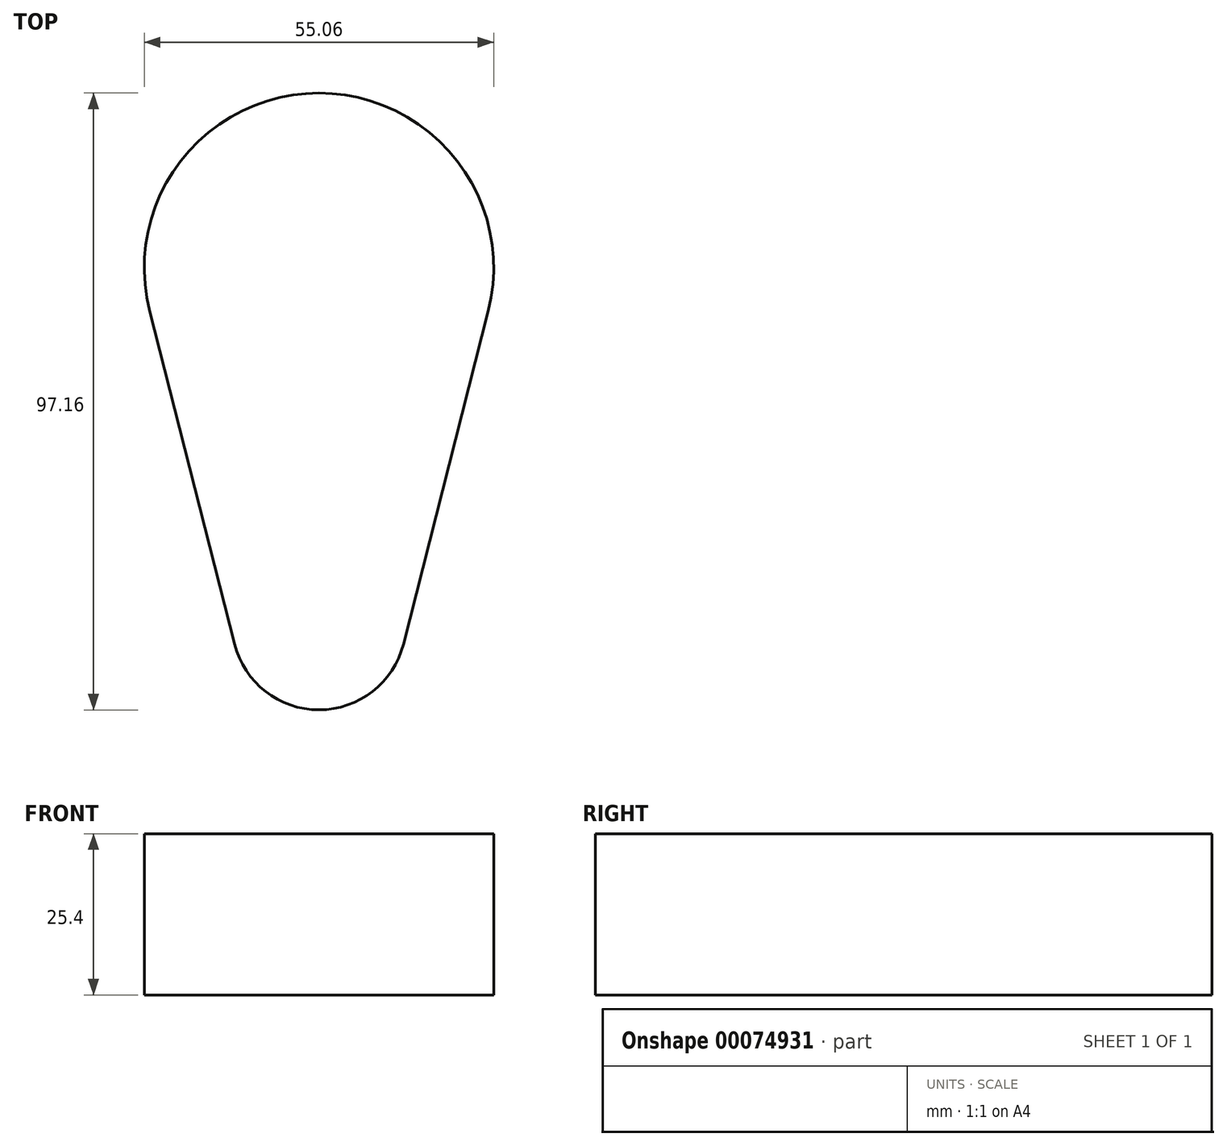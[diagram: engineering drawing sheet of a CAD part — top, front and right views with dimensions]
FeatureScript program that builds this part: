
annotation { "Feature Type Name" : "Feature", "Feature Type Description" : "" }
export const myFeature = defineFeature(function(context is Context, id is Id, definition is map)
    precondition{}
    {
        {
            var Q0;
            Q0=qCreatedBy(makeId("Top.planeOp"),FACE);
            var sketch = newSketch(context, id + "F0", { "sketchPlane" : qUnion([Q0])});
            skArc(sketch, "E0", {"start": v(-13.3, -59.29) * mm, "mid": v(0, -69.63) * mm, "end": v(13.3, -59.29) * mm});
            skLineSegment(sketch, "E1", {"start": v(26.68, -6.8) * mm, "end": v(13.3, -59.29) * mm});
            skLineSegment(sketch, "E2", {"start": v(-13.3, -59.29) * mm, "end": v(-26.68, -6.8) * mm});
            skArc(sketch, "E3", {"start": v(26.68, -6.8) * mm, "mid": v(0, 27.53) * mm, "end": v(-26.68, -6.8) * mm});
            skSolve(sketch);
        }
        {
            var Q0;
            Q0=makeQuery(id+"F0.imprint","IMPRINT",FACE,{"disambiguationData":[TD([[makeQuery(id+"F0.imprint","IMPRINT",EDGE,{"derivedFrom":sQuery(id+"F0.wireOp",EDGE,"8079261a-b3d4-4eea-ad9c-87b29af751e1")}),-1.0]])]});
            var Q1;
            {var subQ0=sQuery(id+"F0.wireOp",EDGE,"E0");var subQ1=makeQuery(id+"F0.imprint","INTERSECT",VERTEX,{"derivedFrom":[subQ0,sQuery(id+"F0.wireOp",EDGE,"E1")]});Q1=makeQuery(id+"F0.imprint","IMPRINT",FACE,{"disambiguationData":[TD([[makeQuery(id+"F0.imprint","IMPRINT",EDGE,{"disambiguationData":[TD([[subQ1,1.0]])],"derivedFrom":subQ0}),1.0]])]});}
            extrude(context, id + "F1", {"entities" : qUnion([Q0, Q1]), "endBound" : BoundingType.SYMMETRIC, "depth" : 25.4 * mm});
        }
    });
